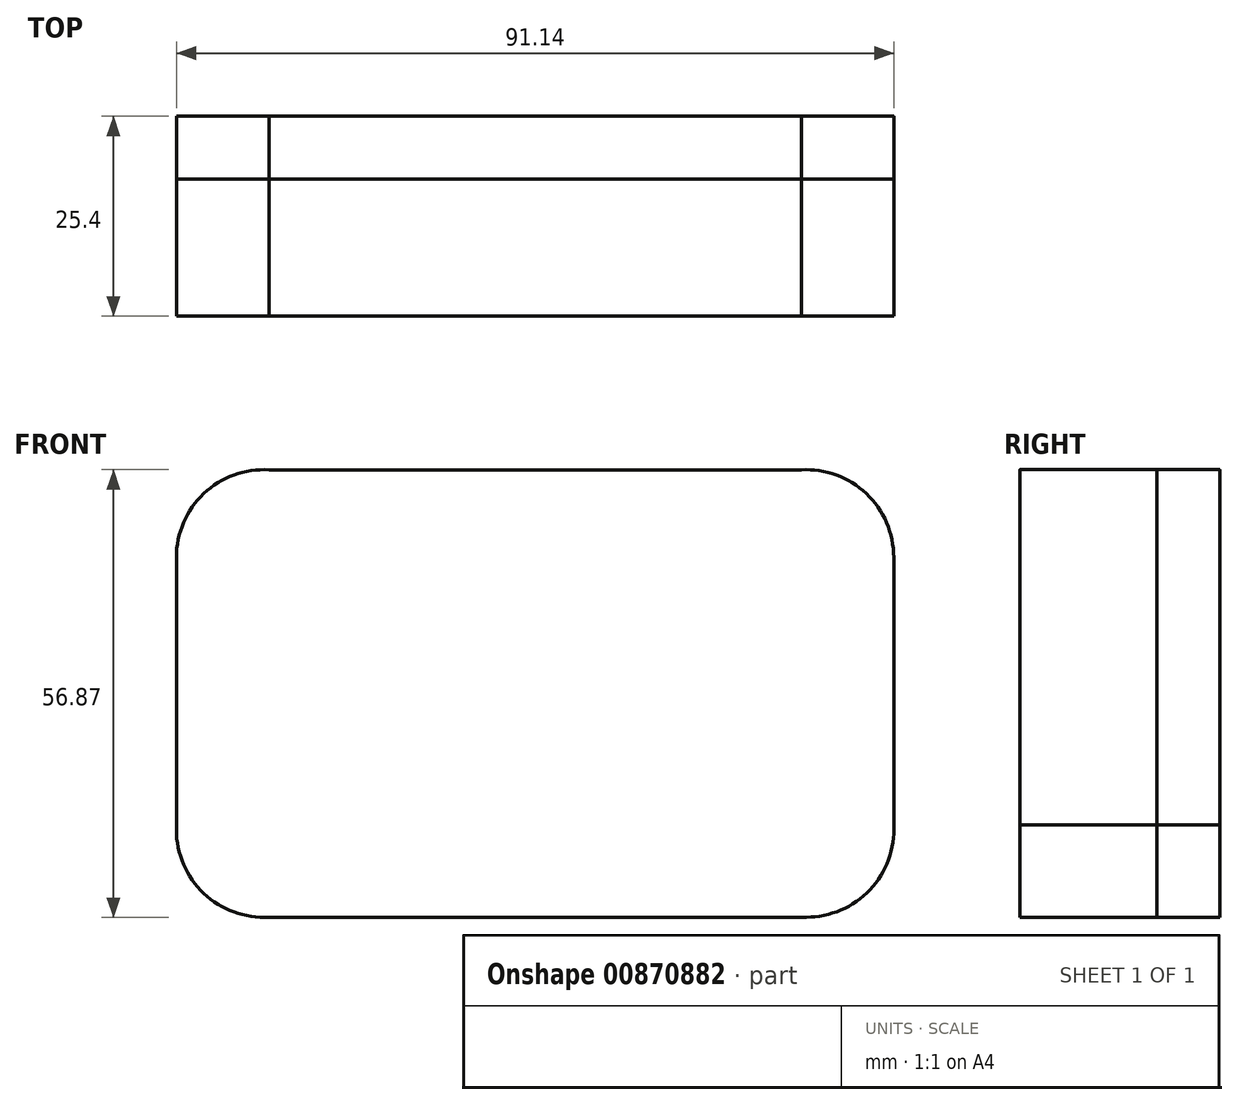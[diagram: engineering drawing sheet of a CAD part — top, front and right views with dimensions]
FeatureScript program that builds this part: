
annotation { "Feature Type Name" : "Feature", "Feature Type Description" : "" }
export const myFeature = defineFeature(function(context is Context, id is Id, definition is map)
    precondition{}
    {
        {
            var Q0;
            Q0=qCreatedBy(makeId("Front.planeOp"),FACE);
            var sketch = newSketch(context, id + "F0", { "sketchPlane" : qUnion([Q0])});
            skLineSegment(sketch, "E0", {"start": v(-33.46, 38.35) * mm, "end": v(34.17, 38.35) * mm});
            skArc(sketch, "E1", {"start": v(45.92, 27.24) * mm, "mid": v(42.44, 35.32) * mm, "end": v(34.17, 38.35) * mm});
            skLineSegment(sketch, "E2", {"start": v(45.92, 27.24) * mm, "end": v(45.92, -6.74) * mm});
            skArc(sketch, "E3", {"start": v(34.8, -18.48) * mm, "mid": v(42.9, -15) * mm, "end": v(45.92, -6.74) * mm});
            skLineSegment(sketch, "E4", {"start": v(34.8, -18.48) * mm, "end": v(-33.46, -18.48) * mm});
            skArc(sketch, "E5", {"start": v(-45.2, -7.37) * mm, "mid": v(-41.72, -15.46) * mm, "end": v(-33.46, -18.48) * mm});
            skLineSegment(sketch, "E6", {"start": v(-45.2, -7.37) * mm, "end": v(-45.2, 27.24) * mm});
            skArc(sketch, "E7", {"start": v(-45.2, 27.24) * mm, "mid": v(-41.72, 35.32) * mm, "end": v(-33.46, 38.35) * mm});
            skArc(sketch, "E8", {"start": v(-34.07, 0) * mm, "mid": v(-28.86, -2.16) * mm, "end": v(-26.7, -7.37) * mm});
            skArc(sketch, "E9", {"start": v(34.8, 0) * mm, "mid": v(29.6, -2.16) * mm, "end": v(27.45, -7.36) * mm});
            skArc(sketch, "E10", {"start": v(-34.07, 19.86) * mm, "mid": v(-28.86, 22.02) * mm, "end": v(-26.7, 27.24) * mm});
            skArc(sketch, "E11", {"start": v(34.8, 19.86) * mm, "mid": v(29.58, 22.02) * mm, "end": v(27.42, 27.24) * mm});
            skLineSegment(sketch, "E12", {"start": v(-26.7, 27.24) * mm, "end": v(27.42, 27.24) * mm});
            skLineSegment(sketch, "E13", {"start": v(34.8, 19.86) * mm, "end": v(34.8, 0) * mm});
            skLineSegment(sketch, "E14", {"start": v(27.45, -7.36) * mm, "end": v(-26.7, -7.37) * mm});
            skLineSegment(sketch, "E15", {"start": v(-34.07, 0) * mm, "end": v(-34.07, 19.86) * mm});
            skCircle(sketch, "E16", {"center": v(-34.07, 27.24) * mm, "radius": 3.69 * mm});
            skCircle(sketch, "E17", {"center": v(-34.07, -7.37) * mm, "radius": 3.74 * mm});
            skCircle(sketch, "E18", {"center": v(34.8, 27.24) * mm, "radius": 3.73 * mm});
            skCircle(sketch, "E19", {"center": v(34.8, -7.35) * mm, "radius": 3.72 * mm});
            skCircle(sketch, "E20", {"center": v(0, 10.33) * mm, "radius": 16.74 * mm});
            skCircle(sketch, "E21", {"center": v(0, 10.33) * mm, "radius": 14.7 * mm});
            skCircle(sketch, "E22", {"center": v(0, 10.33) * mm, "radius": 10.33 * mm});
            skSolve(sketch);
        }
        {
            var Q0;
            Q0=sQuery(id+"F0.wireOp",EDGE,"E0");
            var Q1;
            Q1=sQuery(id+"F0.wireOp",EDGE,"E7");
            var Q2;
            Q2=sQuery(id+"F0.wireOp",EDGE,"E6");
            var Q3;
            Q3=sQuery(id+"F0.wireOp",EDGE,"E5");
            var Q4;
            Q4=sQuery(id+"F0.wireOp",EDGE,"E4");
            var Q5;
            Q5=sQuery(id+"F0.wireOp",EDGE,"E3");
            var Q6;
            Q6=sQuery(id+"F0.wireOp",EDGE,"E2");
            var Q7;
            Q7=sQuery(id+"F0.wireOp",EDGE,"E1");
            extrude(context, id + "F1", {"bodyType" : ToolBodyType.SURFACE, "surfaceEntities" : qUnion([Q0, Q1, Q2, Q3, Q4, Q5, Q6, Q7]), "depth" : 8 * mm, "offsetDistance" : 25.4 * mm});
        }
        {
            var Q0;
            Q0=sQuery(id+"F0.wireOp",EDGE,"E7");
            var Q1;
            Q1=sQuery(id+"F0.wireOp",EDGE,"E0");
            var Q2;
            Q2=sQuery(id+"F0.wireOp",EDGE,"E1");
            var Q3;
            Q3=sQuery(id+"F0.wireOp",EDGE,"E2");
            var Q4;
            Q4=sQuery(id+"F0.wireOp",EDGE,"E3");
            var Q5;
            Q5=sQuery(id+"F0.wireOp",EDGE,"E4");
            var Q6;
            Q6=sQuery(id+"F0.wireOp",EDGE,"E5");
            var Q7;
            Q7=sQuery(id+"F0.wireOp",EDGE,"E6");
            extrude(context, id + "F2", {"bodyType" : ToolBodyType.SURFACE, "surfaceEntities" : qUnion([Q0, Q1, Q2, Q3, Q4, Q5, Q6, Q7]), "depth" : 25.4 * mm, "offsetDistance" : 25.4 * mm});
        }
    });
